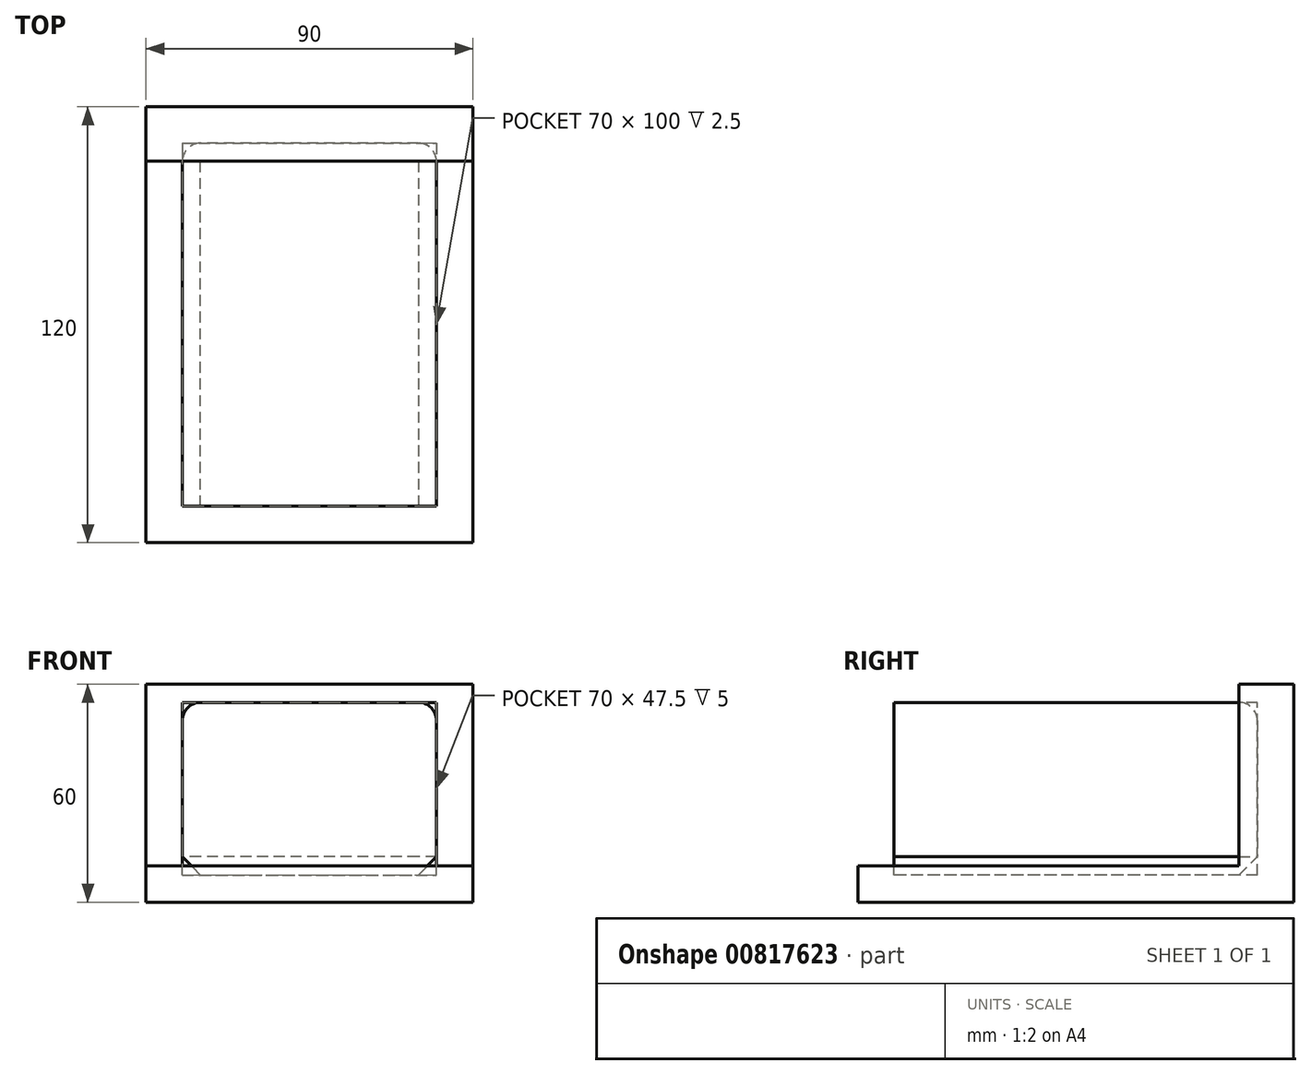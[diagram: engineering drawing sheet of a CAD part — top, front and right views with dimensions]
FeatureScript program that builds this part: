
annotation { "Feature Type Name" : "Feature", "Feature Type Description" : "" }
export const myFeature = defineFeature(function(context is Context, id is Id, definition is map)
    precondition{}
    {
        {
            var Q0;
            Q0=qCreatedBy(makeId("Top.planeOp"),FACE);
            var sketch = newSketch(context, id + "F0", { "sketchPlane" : qUnion([Q0])});
            skLineSegment(sketch, "E0.bottom", {"start": v(0, 0) * mm, "end": v(90, 0) * mm});
            skLineSegment(sketch, "E0.top", {"start": v(0, 120) * mm, "end": v(90, 120) * mm});
            skLineSegment(sketch, "E0.left", {"start": v(0, 0) * mm, "end": v(0, 120) * mm});
            skLineSegment(sketch, "E0.right", {"start": v(90, 0) * mm, "end": v(90, 120) * mm});
            skSolve(sketch);
        }
        {
            var Q0;
            Q0 = qSketchRegion(id + "F0", true);
            extrude(context, id + "F1", {"entities" : qUnion([Q0]), "depth" : 10 * mm, "offsetDistance" : 25 * mm});
        }
        {
            var Q0;
            Q0=makeQuery(id+"F1.opExtrude","CAP_FACE",FACE,{"disambiguationData":[OSD([sQuery(id+"F0.wireOp",EDGE,"E0.bottom"),sQuery(id+"F0.wireOp",EDGE,"E0.top"),sQuery(id+"F0.wireOp",EDGE,"E0.left"),sQuery(id+"F0.wireOp",EDGE,"E0.right")])],"isStart":false});
            var sketch = newSketch(context, id + "F2", { "sketchPlane" : qUnion([Q0])});
            skLineSegment(sketch, "E1", {"start": v(0, 105) * mm, "end": v(90, 105) * mm});
            skSolve(sketch);
        }
        {
            var Q0;
            {var subQ0=sQuery(id+"F2.wireOp",EDGE,"E1");Q0=makeQuery(id+"F2.imprint","IMPRINT",FACE,{"disambiguationData":[TD([[makeQuery(id+"F2.imprint","IMPRINT",EDGE,{"derivedFrom":subQ0}),1.0]])]});}
            extrude(context, id + "F3", {"entities" : qUnion([Q0]), "operationType" : NewBodyOperationType.ADD, "depth" : 50 * mm, "offsetDistance" : 25 * mm});
        }
        {
            var Q0;
            Q0=makeQuery(id+"F3.opExtrude","CAP_FACE",FACE,{"disambiguationData":[OSD([sQuery(id+"F0.wireOp",EDGE,"E0.top"),sQuery(id+"F0.wireOp",EDGE,"E0.left"),sQuery(id+"F0.wireOp",EDGE,"E0.right"),sQuery(id+"F2.wireOp",EDGE,"E1")])],"isStart":false});
            cPlane(context, id + "F4", {"entities" : qUnion([Q0]), "cplaneType" : CPlaneType.OFFSET, "offset" : 5 * mm, "oppositeDirection" : true, "width" : 150 * mm, "height" : 150 * mm});
        }
        {
            var Q0;
            Q0=qCreatedBy(id+"F4.planeOp",FACE);
            var sketch = newSketch(context, id + "F5", { "sketchPlane" : qUnion([Q0])});
            skLineSegment(sketch, "E2.bottom", {"start": v(10, 110) * mm, "end": v(80, 110) * mm});
            skLineSegment(sketch, "E2.top", {"start": v(10, 10) * mm, "end": v(80, 10) * mm});
            skLineSegment(sketch, "E2.left", {"start": v(10, 110) * mm, "end": v(10, 10) * mm});
            skLineSegment(sketch, "E2.right", {"start": v(80, 110) * mm, "end": v(80, 10) * mm});
            skSolve(sketch);
        }
        {
            var Q0;
            {var subQ0=sQuery(id+"F5.wireOp",EDGE,"E2.top");Q0=makeQuery(id+"F5.imprint","IMPRINT",FACE,{"disambiguationData":[TD([[makeQuery(id+"F5.imprint","IMPRINT",EDGE,{"derivedFrom":subQ0}),1.0]])]});}
            var Q1;
            {var subQ0=sQuery(id+"F5.wireOp",EDGE,"E2.bottom");Q1=makeQuery(id+"F5.imprint","IMPRINT",FACE,{"disambiguationData":[TD([[makeQuery(id+"F5.imprint","IMPRINT",EDGE,{"derivedFrom":subQ0}),-1.0]])]});}
            extrude(context, id + "F6", {"entities" : qUnion([Q0, Q1]), "operationType" : NewBodyOperationType.REMOVE, "oppositeDirection" : true, "depth" : 47.5 * mm, "offsetDistance" : 25 * mm});
        }
        {
            var Q0;
            Q0=makeQuery(id+"F6.boolean.opBoolean","COPY",FACE,{"derivedFrom":makeQuery(id+"F6.opExtrude","CAP_FACE",FACE,{"disambiguationData":[OSD([sQuery(id+"F5.wireOp",EDGE,"E2.bottom"),sQuery(id+"F5.wireOp",EDGE,"E2.top"),sQuery(id+"F5.wireOp",EDGE,"E2.left"),sQuery(id+"F5.wireOp",EDGE,"E2.right")])],"isStart":false})});
            var Q1;
            Q1=makeQuery(id+"F6.boolean.opBoolean","COPY",FACE,{"derivedFrom":makeQuery(id+"F6.opExtrude","CAP_FACE",FACE,{"disambiguationData":[OSD([sQuery(id+"F5.wireOp",EDGE,"E2.bottom"),sQuery(id+"F5.wireOp",EDGE,"E2.top"),sQuery(id+"F5.wireOp",EDGE,"E2.left"),sQuery(id+"F5.wireOp",EDGE,"E2.right")])],"isStart":true})});
            extrude(context, id + "F7", {"entities" : qUnion([Q0]), "endBound" : BoundingType.UP_TO_SURFACE, "depth" : 40.5 * mm, "endBoundEntityFace" : qUnion([Q1]), "offsetDistance" : 25 * mm});
        }
        {
            var Q0;
            Q0=makeQuery(id+"F7.opExtrude","CAP_EDGE",EDGE,{"disambiguationData":[OSD([sQuery(id+"F5.wireOp",EDGE,"E2.right")])],"isStart":false});
            var Q1;
            Q1=makeQuery(id+"F7.opExtrude","CAP_EDGE",EDGE,{"disambiguationData":[OSD([sQuery(id+"F5.wireOp",EDGE,"E2.left")])],"isStart":false});
            var Q2;
            Q2=makeQuery(id+"F7.opExtrude","SWEPT_EDGE",EDGE,{"disambiguationData":[OSD([sQuery(id+"F5.wireOp",EDGE,"E2.bottom"),sQuery(id+"F5.wireOp",EDGE,"E2.right")])]});
            var Q3;
            Q3=makeQuery(id+"F7.opExtrude","CAP_EDGE",EDGE,{"disambiguationData":[OSD([sQuery(id+"F5.wireOp",EDGE,"E2.bottom")])],"isStart":false});
            var Q4;
            Q4=makeQuery(id+"F7.opExtrude","SWEPT_EDGE",EDGE,{"disambiguationData":[OSD([sQuery(id+"F5.wireOp",EDGE,"E2.bottom"),sQuery(id+"F5.wireOp",EDGE,"E2.left")])]});
            fillet(context, id + "F8", {"entities" : qUnion([Q0, Q1, Q2, Q3, Q4]), "radius" : 5 * mm, "tangentPropagation" : true, "allowEdgeOverflow" : false});
        }
        {
            var Q0;
            Q0=makeQuery(id+"F7.opExtrude","CAP_EDGE",EDGE,{"disambiguationData":[OSD([sQuery(id+"F5.wireOp",EDGE,"E2.right")])],"isStart":true});
            var Q1;
            Q1=makeQuery(id+"F7.opExtrude","CAP_EDGE",EDGE,{"disambiguationData":[OSD([sQuery(id+"F5.wireOp",EDGE,"E2.left")])],"isStart":true});
            chamfer(context, id + "F9", {"entities" : qUnion([Q0, Q1]), "width" : 5 * mm, "tangentPropagation" : true});
        }
    });
